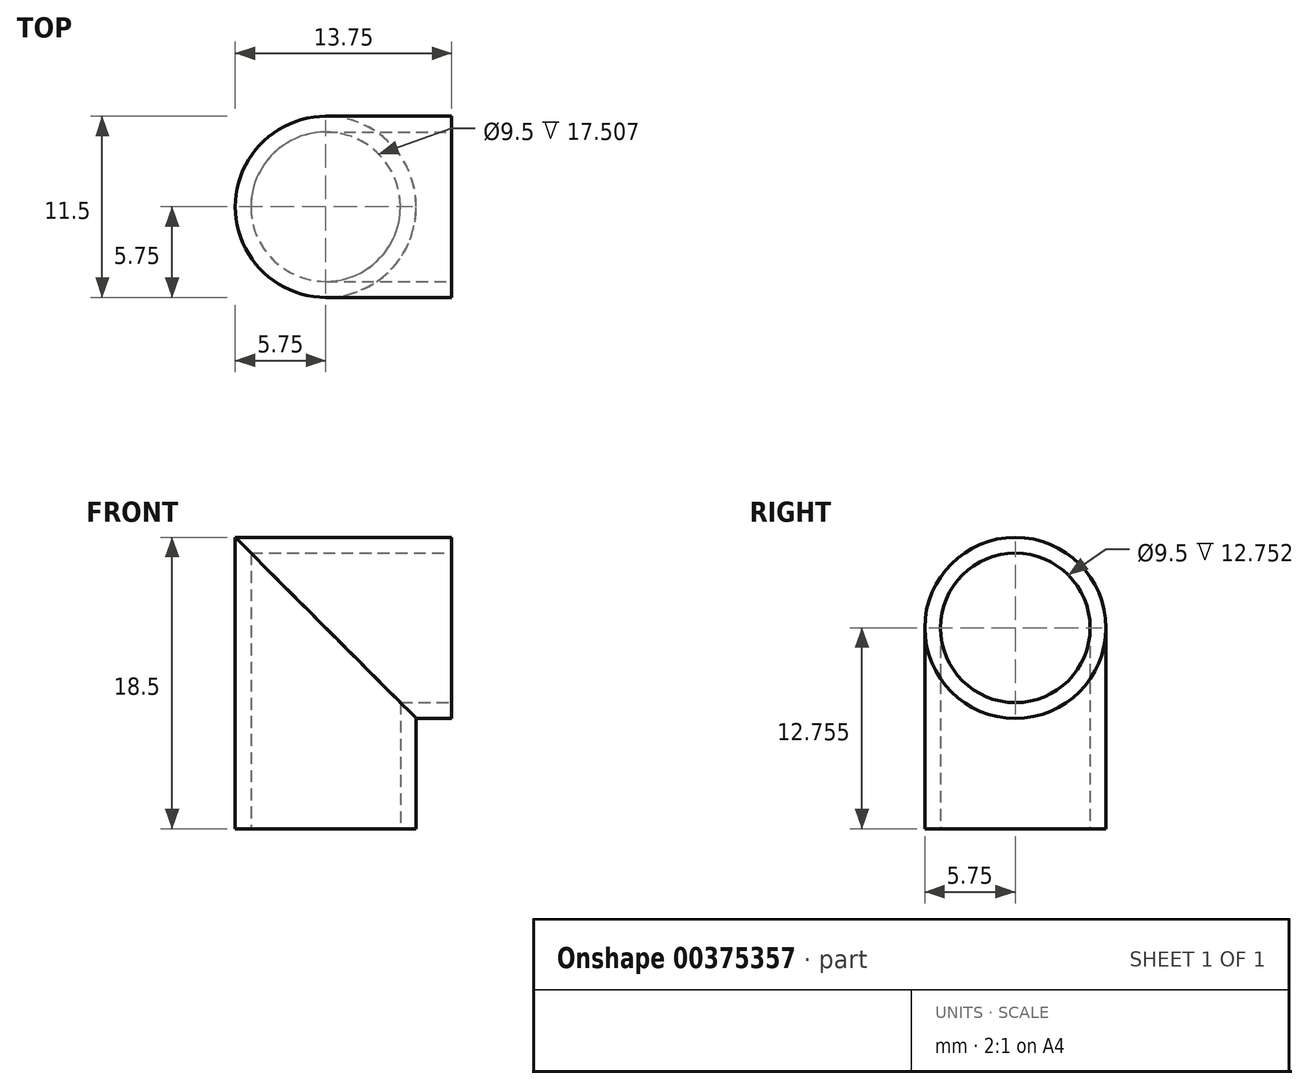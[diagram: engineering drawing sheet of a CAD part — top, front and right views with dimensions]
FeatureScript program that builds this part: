
annotation { "Feature Type Name" : "Feature", "Feature Type Description" : "" }
export const myFeature = defineFeature(function(context is Context, id is Id, definition is map)
    precondition{}
    {
        {
            var Q0;
            Q0=qCreatedBy(makeId("Top.planeOp"),FACE);
            var sketch = newSketch(context, id + "F0", { "sketchPlane" : qUnion([Q0])});
            skCircle(sketch, "E0", {"center": v(0, 0) * mm, "radius": 5.75 * mm});
            skCircle(sketch, "E1", {"center": v(0, 0) * mm, "radius": 4.75 * mm});
            skSolve(sketch);
        }
        {
            var Q0;
            Q0=makeQuery(id+"F0.imprint","IMPRINT",FACE,{"disambiguationData":[TD([[makeQuery(id+"F0.imprint","IMPRINT",EDGE,{"derivedFrom":sQuery(id+"F0.wireOp",EDGE,"E0")}),1.0]])]});
            extrude(context, id + "F1", {"entities" : qUnion([Q0]), "depth" : 4 * mm});
        }
        {
            var Q0;
            Q0=qCreatedBy(makeId("Right.planeOp"),FACE);
            cPlane(context, id + "F2", {"entities" : qUnion([Q0]), "cplaneType" : CPlaneType.OFFSET, "offset" : 8 * mm, "width" : 150 * mm, "height" : 150 * mm});
        }
        {
            var Q0;
            Q0=qCreatedBy(id+"F2.planeOp",FACE);
            var sketch = newSketch(context, id + "F3", { "sketchPlane" : qUnion([Q0])});
            skCircle(sketch, "E2", {"center": v(0, 12.75) * mm, "radius": 5.75 * mm});
            skCircle(sketch, "E3", {"center": v(0, 12.75) * mm, "radius": 4.75 * mm});
            skSolve(sketch);
        }
        {
            var Q0;
            Q0=qCreatedBy(makeId("Front.planeOp"),FACE);
            var sketch = newSketch(context, id + "F4", { "sketchPlane" : qUnion([Q0])});
            skPoint(sketch, "E4.0", {"position": v(8, 12.75) * mm});
            skLineSegment(sketch, "E5.0", {"start": v(-5.75, 4) * mm, "end": v(5.75, 4) * mm});
            skLineSegment(sketch, "E6", {"start": v(0, 4) * mm, "end": v(0, 12.75) * mm});
            skLineSegment(sketch, "E7", {"start": v(0, 12.75) * mm, "end": v(8, 12.75) * mm});
            skSolve(sketch);
        }
        {
            var Q0;
            Q0=makeQuery(id+"F1.opExtrude","CAP_FACE",FACE,{"disambiguationData":[OSD([sQuery(id+"F0.wireOp",EDGE,"E0"),sQuery(id+"F0.wireOp",EDGE,"E1")])],"isStart":false});
            var Q1;
            Q1=sQuery(id+"F4.wireOp",EDGE,"E6");
            var Q2;
            Q2=sQuery(id+"F4.wireOp",EDGE,"E7");
            sweep(context, id + "F5", {"operationType" : NewBodyOperationType.ADD, "profiles" : qUnion([Q0]), "path" : qUnion([Q1, Q2])});
        }
    });
